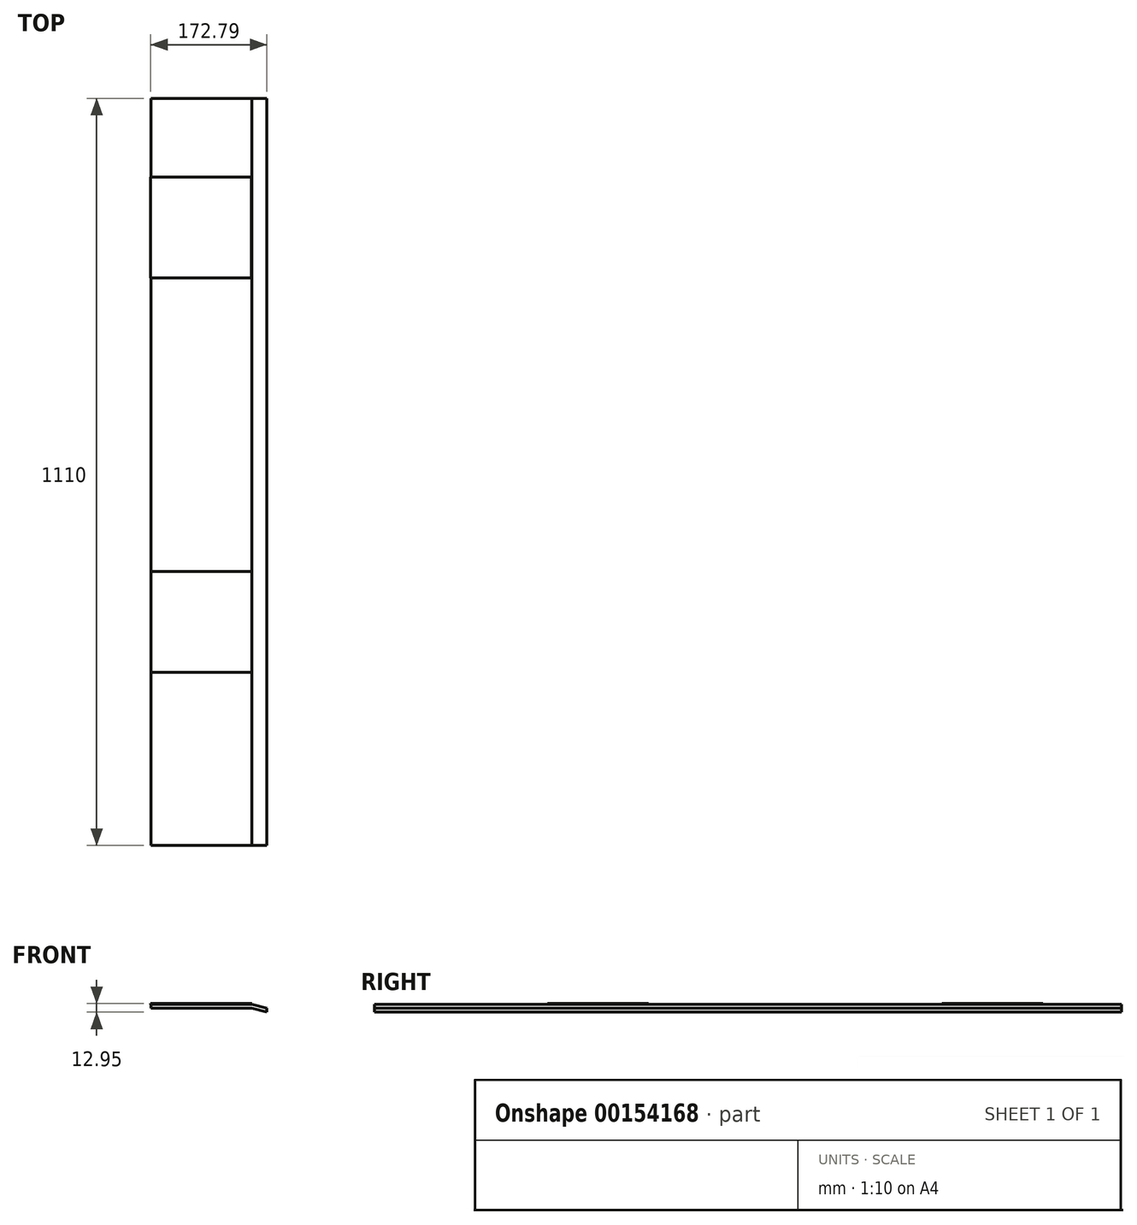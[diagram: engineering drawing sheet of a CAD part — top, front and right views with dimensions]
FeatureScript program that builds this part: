
annotation { "Feature Type Name" : "Feature", "Feature Type Description" : "" }
export const myFeature = defineFeature(function(context is Context, id is Id, definition is map)
    precondition{}
    {
        {
            var Q0;
            Q0=qCreatedBy(makeId("Front.planeOp"),FACE);
            var sketch = newSketch(context, id + "F0", { "sketchPlane" : qUnion([Q0])});
            skLineSegment(sketch, "E0", {"start": v(0, 0) * mm, "end": v(150, 0) * mm});
            skLineSegment(sketch, "E1", {"start": v(150, 0) * mm, "end": v(172.22, -5.95) * mm});
            skLineSegment(sketch, "E2", {"start": v(0, 0) * mm, "end": v(0, -6) * mm});
            skLineSegment(sketch, "E3", {"start": v(0, -6) * mm, "end": v(150, -6) * mm});
            skLineSegment(sketch, "E4", {"start": v(150, -6) * mm, "end": v(172.22, -11.95) * mm});
            skLineSegment(sketch, "E5", {"start": v(172.22, -11.95) * mm, "end": v(172.22, -5.95) * mm});
            skSolve(sketch);
        }
        {
            var Q0;
            Q0=makeQuery(id+"F0.imprint","IMPRINT",FACE,{"disambiguationData":[TD([[makeQuery(id+"F0.imprint","IMPRINT",EDGE,{"derivedFrom":sQuery(id+"F0.wireOp",EDGE,"E0")}),-1.0]])]});
            extrude(context, id + "F1", {"entities" : qUnion([Q0]), "depth" : 1110 * mm});
        }
        {
            var Q0;
            Q0=makeQuery(id+"F1.opExtrude","SWEPT_FACE",FACE,{"disambiguationData":[OSD([sQuery(id+"F0.wireOp",EDGE,"E0")])]});
            var sketch = newSketch(context, id + "F2", { "sketchPlane" : qUnion([Q0])});
            skLineSegment(sketch, "E6.bottom", {"start": v(149.43, -267.02) * mm, "end": v(-0.57, -267.02) * mm});
            skLineSegment(sketch, "E6.top", {"start": v(149.43, -117.02) * mm, "end": v(-0.57, -117.02) * mm});
            skLineSegment(sketch, "E6.left", {"start": v(149.43, -267.02) * mm, "end": v(149.43, -117.02) * mm});
            skLineSegment(sketch, "E6.right", {"start": v(-0.57, -267.02) * mm, "end": v(-0.57, -117.02) * mm});
            skPoint(sketch, "E6.middle", {"position": v(74.43, -192.02) * mm});
            skLineSegment(sketch, "E7.bottom", {"start": v(150, -852.97) * mm, "end": v(0, -852.97) * mm});
            skLineSegment(sketch, "E7.top", {"start": v(150, -702.97) * mm, "end": v(0, -702.97) * mm});
            skLineSegment(sketch, "E7.left", {"start": v(150, -852.97) * mm, "end": v(150, -702.97) * mm});
            skLineSegment(sketch, "E7.right", {"start": v(0, -852.97) * mm, "end": v(0, -702.97) * mm});
            skPoint(sketch, "E7.middle", {"position": v(75, -777.97) * mm});
            skSolve(sketch);
        }
        {
            var Q0;
            Q0 = qSketchRegion(id + "F2", true);
            extrude(context, id + "F3", {"entities" : qUnion([Q0]), "operationType" : NewBodyOperationType.ADD, "depth" : 1 * mm});
        }
    });
